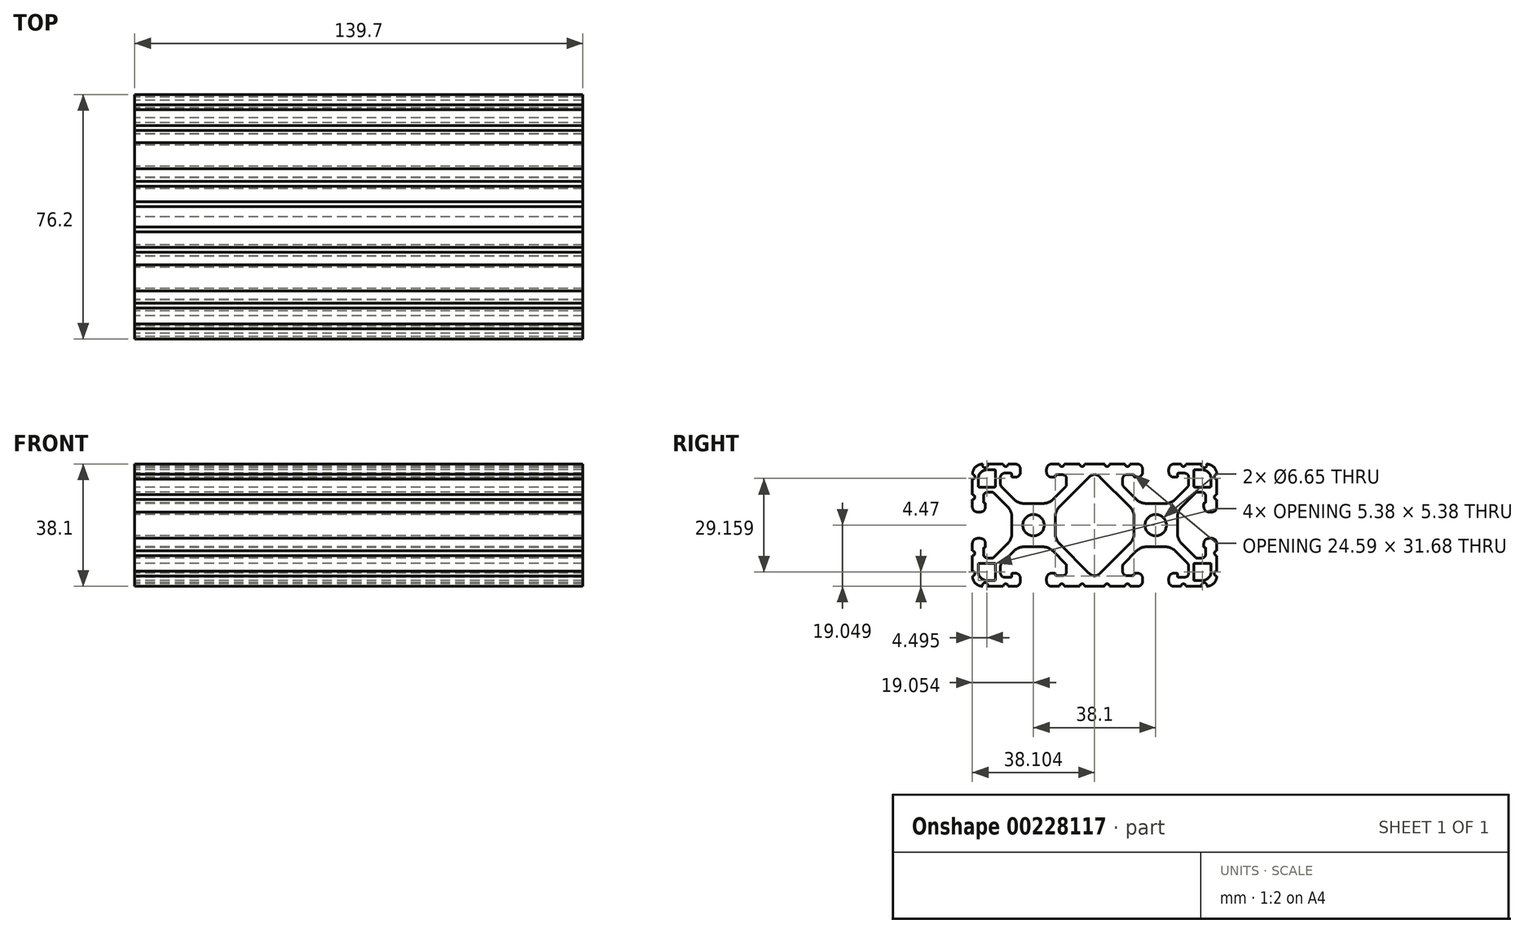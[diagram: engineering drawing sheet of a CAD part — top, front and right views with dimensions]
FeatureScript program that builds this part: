
annotation { "Feature Type Name" : "Feature", "Feature Type Description" : "" }
export const myFeature = defineFeature(function(context is Context, id is Id, definition is map)
    precondition{}
    {
        {
            var Q0;
            Q0=qCreatedBy(makeId("Right.planeOp"),FACE);
            var sketch = newSketch(context, id + "F0", { "sketchPlane" : qUnion([Q0])});
            skArc(sketch, "E0.0.0", {"start": v(-2.87, 19.05) * mm, "mid": v(-3.63, 18.29) * mm, "end": v(-4.4, 19.05) * mm});
            skLineSegment(sketch, "E0.0.1", {"start": v(-4.4, 19.05) * mm, "end": v(-9.22, 19.05) * mm});
            skArc(sketch, "E0.0.2", {"start": v(-9.22, 19.05) * mm, "mid": v(-9.98, 18.29) * mm, "end": v(-10.74, 19.05) * mm});
            skLineSegment(sketch, "E0.0.3", {"start": v(-10.74, 19.05) * mm, "end": v(-13.16, 19.05) * mm});
            skArc(sketch, "E0.0.4", {"start": v(-13.16, 19.05) * mm, "mid": v(-14.27, 18.59) * mm, "end": v(-14.73, 17.47) * mm});
            skLineSegment(sketch, "E0.0.5", {"start": v(-14.73, 17.47) * mm, "end": v(-14.73, 16.56) * mm});
            skArc(sketch, "E0.0.6", {"start": v(-14.73, 16.56) * mm, "mid": v(-14.27, 15.45) * mm, "end": v(-13.16, 14.99) * mm});
            skLineSegment(sketch, "E0.0.7", {"start": v(-13.16, 14.99) * mm, "end": v(-12.22, 14.99) * mm});
            skArc(sketch, "E0.0.8", {"start": v(-12.22, 14.99) * mm, "mid": v(-12.04, 15.06) * mm, "end": v(-11.96, 15.24) * mm});
            skLineSegment(sketch, "E0.0.9", {"start": v(-11.96, 15.24) * mm, "end": v(-11.96, 15.5) * mm});
            skArc(sketch, "E0.0.10", {"start": v(-11.96, 15.5) * mm, "mid": v(-11.89, 15.68) * mm, "end": v(-11.7, 15.75) * mm});
            skLineSegment(sketch, "E0.0.11", {"start": v(-11.7, 15.75) * mm, "end": v(-9.78, 15.75) * mm});
            skArc(sketch, "E0.0.12", {"start": v(-9.78, 15.75) * mm, "mid": v(-8.88, 15.38) * mm, "end": v(-8.5, 14.48) * mm});
            skLineSegment(sketch, "E0.0.13", {"start": v(-8.5, 14.48) * mm, "end": v(-8.5, 12.63) * mm});
            skArc(sketch, "E0.0.14", {"start": v(-8.5, 12.63) * mm, "mid": v(-8.58, 12.3) * mm, "end": v(-8.77, 12) * mm});
            skLineSegment(sketch, "E0.0.15", {"start": v(-8.77, 12) * mm, "end": v(-12.65, 8.12) * mm});
            skArc(sketch, "E0.0.16", {"start": v(-12.65, 8.12) * mm, "mid": v(-14.17, 7.11) * mm, "end": v(-15.95, 6.76) * mm});
            skLineSegment(sketch, "E0.0.17", {"start": v(-15.95, 6.76) * mm, "end": v(-21.69, 6.76) * mm});
            skArc(sketch, "E0.0.18", {"start": v(-21.69, 6.76) * mm, "mid": v(-23.43, 7.1) * mm, "end": v(-24.9, 8.09) * mm});
            skLineSegment(sketch, "E0.0.19", {"start": v(-24.9, 8.09) * mm, "end": v(-28.7, 11.9) * mm});
            skArc(sketch, "E0.0.20", {"start": v(-28.7, 11.9) * mm, "mid": v(-28.99, 12.3) * mm, "end": v(-29.08, 12.8) * mm});
            skLineSegment(sketch, "E0.0.21", {"start": v(-29.08, 12.8) * mm, "end": v(-29.08, 14.95) * mm});
            skArc(sketch, "E0.0.22", {"start": v(-29.08, 14.95) * mm, "mid": v(-28.71, 15.85) * mm, "end": v(-27.81, 16.22) * mm});
            skLineSegment(sketch, "E0.0.23", {"start": v(-27.81, 16.22) * mm, "end": v(-25.88, 16.22) * mm});
            skArc(sketch, "E0.0.24", {"start": v(-25.88, 16.22) * mm, "mid": v(-25.7, 16.14) * mm, "end": v(-25.63, 15.96) * mm});
            skLineSegment(sketch, "E0.0.25", {"start": v(-25.63, 15.96) * mm, "end": v(-25.63, 15.24) * mm});
            skArc(sketch, "E0.0.26", {"start": v(-25.63, 15.24) * mm, "mid": v(-25.56, 15.06) * mm, "end": v(-25.38, 14.99) * mm});
            skLineSegment(sketch, "E0.0.27", {"start": v(-25.38, 14.99) * mm, "end": v(-24.44, 14.99) * mm});
            skArc(sketch, "E0.0.28", {"start": v(-24.44, 14.99) * mm, "mid": v(-23.32, 15.45) * mm, "end": v(-22.86, 16.56) * mm});
            skLineSegment(sketch, "E0.0.29", {"start": v(-22.86, 16.56) * mm, "end": v(-22.86, 17.45) * mm});
            skArc(sketch, "E0.0.30", {"start": v(-22.86, 17.45) * mm, "mid": v(-23.33, 18.58) * mm, "end": v(-24.46, 19.05) * mm});
            skLineSegment(sketch, "E0.0.31", {"start": v(-24.46, 19.05) * mm, "end": v(-26.7, 19.05) * mm});
            skArc(sketch, "E0.0.32", {"start": v(-26.7, 19.05) * mm, "mid": v(-27.45, 18.29) * mm, "end": v(-28.22, 19.05) * mm});
            skLineSegment(sketch, "E0.0.33", {"start": v(-28.22, 19.05) * mm, "end": v(-33.15, 19.05) * mm});
            skArc(sketch, "E0.0.34", {"start": v(-33.15, 19.05) * mm, "mid": v(-33.9, 17.92) * mm, "end": v(-34.64, 19.05) * mm});
            skArc(sketch, "E0.0.35", {"start": v(-34.64, 19.05) * mm, "mid": v(-36.9, 18.11) * mm, "end": v(-37.82, 15.85) * mm});
            skArc(sketch, "E0.0.36", {"start": v(-37.82, 15.85) * mm, "mid": v(-37.07, 15.07) * mm, "end": v(-37.85, 14.32) * mm});
            skLineSegment(sketch, "E0.0.37", {"start": v(-37.85, 14.32) * mm, "end": v(-37.85, 9.5) * mm});
            skArc(sketch, "E0.0.38", {"start": v(-37.85, 9.5) * mm, "mid": v(-37.08, 8.73) * mm, "end": v(-37.85, 7.97) * mm});
            skLineSegment(sketch, "E0.0.39", {"start": v(-37.85, 7.97) * mm, "end": v(-37.85, 5.64) * mm});
            skArc(sketch, "E0.0.40", {"start": v(-37.85, 5.64) * mm, "mid": v(-37.4, 4.56) * mm, "end": v(-36.31, 4.11) * mm});
            skLineSegment(sketch, "E0.0.41", {"start": v(-36.31, 4.11) * mm, "end": v(-35.36, 4.11) * mm});
            skArc(sketch, "E0.0.42", {"start": v(-35.36, 4.11) * mm, "mid": v(-34.24, 4.57) * mm, "end": v(-33.78, 5.69) * mm});
            skLineSegment(sketch, "E0.0.43", {"start": v(-33.78, 5.69) * mm, "end": v(-33.78, 6.7) * mm});
            skArc(sketch, "E0.0.44", {"start": v(-33.78, 6.7) * mm, "mid": v(-33.86, 6.88) * mm, "end": v(-34.04, 6.96) * mm});
            skLineSegment(sketch, "E0.0.45", {"start": v(-34.04, 6.96) * mm, "end": v(-34.14, 6.96) * mm});
            skArc(sketch, "E0.0.46", {"start": v(-34.14, 6.96) * mm, "mid": v(-34.32, 7.03) * mm, "end": v(-34.4, 7.21) * mm});
            skLineSegment(sketch, "E0.0.47", {"start": v(-34.4, 7.21) * mm, "end": v(-34.4, 9.03) * mm});
            skArc(sketch, "E0.0.48", {"start": v(-34.4, 9.03) * mm, "mid": v(-34.02, 9.92) * mm, "end": v(-33.13, 10.3) * mm});
            skLineSegment(sketch, "E0.0.49", {"start": v(-33.13, 10.3) * mm, "end": v(-31.78, 10.3) * mm});
            skArc(sketch, "E0.0.50", {"start": v(-31.78, 10.3) * mm, "mid": v(-31.45, 10.22) * mm, "end": v(-31.17, 10.04) * mm});
            skLineSegment(sketch, "E0.0.51", {"start": v(-31.17, 10.04) * mm, "end": v(-26.94, 5.82) * mm});
            skArc(sketch, "E0.0.52", {"start": v(-26.94, 5.82) * mm, "mid": v(-25.91, 4.27) * mm, "end": v(-25.55, 2.46) * mm});
            skLineSegment(sketch, "E0.0.53", {"start": v(-25.55, 2.46) * mm, "end": v(-25.55, -2.46) * mm});
            skArc(sketch, "E0.0.54", {"start": v(-25.55, -2.46) * mm, "mid": v(-25.91, -4.28) * mm, "end": v(-26.94, -5.82) * mm});
            skLineSegment(sketch, "E0.0.55", {"start": v(-26.94, -5.82) * mm, "end": v(-31.17, -10.04) * mm});
            skArc(sketch, "E0.0.56", {"start": v(-31.17, -10.04) * mm, "mid": v(-31.45, -10.23) * mm, "end": v(-31.78, -10.3) * mm});
            skLineSegment(sketch, "E0.0.57", {"start": v(-31.78, -10.3) * mm, "end": v(-33.13, -10.3) * mm});
            skArc(sketch, "E0.0.58", {"start": v(-33.13, -10.3) * mm, "mid": v(-34.02, -9.92) * mm, "end": v(-34.4, -9.03) * mm});
            skLineSegment(sketch, "E0.0.59", {"start": v(-34.4, -9.03) * mm, "end": v(-34.4, -7.21) * mm});
            skArc(sketch, "E0.0.60", {"start": v(-34.4, -7.21) * mm, "mid": v(-34.32, -7.03) * mm, "end": v(-34.14, -6.96) * mm});
            skLineSegment(sketch, "E0.0.61", {"start": v(-34.14, -6.96) * mm, "end": v(-34.04, -6.96) * mm});
            skArc(sketch, "E0.0.62", {"start": v(-34.04, -6.96) * mm, "mid": v(-33.86, -6.89) * mm, "end": v(-33.78, -6.7) * mm});
            skLineSegment(sketch, "E0.0.63", {"start": v(-33.78, -6.7) * mm, "end": v(-33.78, -5.69) * mm});
            skArc(sketch, "E0.0.64", {"start": v(-33.78, -5.69) * mm, "mid": v(-34.24, -4.57) * mm, "end": v(-35.36, -4.11) * mm});
            skLineSegment(sketch, "E0.0.65", {"start": v(-35.36, -4.11) * mm, "end": v(-36.31, -4.11) * mm});
            skArc(sketch, "E0.0.66", {"start": v(-36.31, -4.11) * mm, "mid": v(-37.4, -4.56) * mm, "end": v(-37.85, -5.65) * mm});
            skLineSegment(sketch, "E0.0.67", {"start": v(-37.85, -5.65) * mm, "end": v(-37.85, -7.97) * mm});
            skArc(sketch, "E0.0.68", {"start": v(-37.85, -7.97) * mm, "mid": v(-37.08, -8.74) * mm, "end": v(-37.85, -9.5) * mm});
            skLineSegment(sketch, "E0.0.69", {"start": v(-37.85, -9.5) * mm, "end": v(-37.85, -14.33) * mm});
            skArc(sketch, "E0.0.70", {"start": v(-37.85, -14.33) * mm, "mid": v(-37.07, -15.08) * mm, "end": v(-37.82, -15.85) * mm});
            skArc(sketch, "E0.0.71", {"start": v(-37.82, -15.85) * mm, "mid": v(-36.9, -18.12) * mm, "end": v(-34.64, -19.05) * mm});
            skArc(sketch, "E0.0.72", {"start": v(-34.64, -19.05) * mm, "mid": v(-33.9, -17.92) * mm, "end": v(-33.15, -19.05) * mm});
            skLineSegment(sketch, "E0.0.73", {"start": v(-33.15, -19.05) * mm, "end": v(-28.22, -19.05) * mm});
            skArc(sketch, "E0.0.74", {"start": v(-28.22, -19.05) * mm, "mid": v(-27.45, -18.29) * mm, "end": v(-26.7, -19.05) * mm});
            skLineSegment(sketch, "E0.0.75", {"start": v(-26.7, -19.05) * mm, "end": v(-24.46, -19.05) * mm});
            skArc(sketch, "E0.0.76", {"start": v(-24.46, -19.05) * mm, "mid": v(-23.33, -18.58) * mm, "end": v(-22.86, -17.45) * mm});
            skLineSegment(sketch, "E0.0.77", {"start": v(-22.86, -17.45) * mm, "end": v(-22.86, -16.56) * mm});
            skArc(sketch, "E0.0.78", {"start": v(-22.86, -16.56) * mm, "mid": v(-23.32, -15.45) * mm, "end": v(-24.44, -14.99) * mm});
            skLineSegment(sketch, "E0.0.79", {"start": v(-24.44, -14.99) * mm, "end": v(-25.38, -14.99) * mm});
            skArc(sketch, "E0.0.80", {"start": v(-25.38, -14.99) * mm, "mid": v(-25.56, -15.06) * mm, "end": v(-25.63, -15.24) * mm});
            skLineSegment(sketch, "E0.0.81", {"start": v(-25.63, -15.24) * mm, "end": v(-25.63, -15.97) * mm});
            skArc(sketch, "E0.0.82", {"start": v(-25.63, -15.97) * mm, "mid": v(-25.7, -16.15) * mm, "end": v(-25.88, -16.22) * mm});
            skLineSegment(sketch, "E0.0.83", {"start": v(-25.88, -16.22) * mm, "end": v(-27.81, -16.22) * mm});
            skArc(sketch, "E0.0.84", {"start": v(-27.81, -16.22) * mm, "mid": v(-28.71, -15.85) * mm, "end": v(-29.08, -14.95) * mm});
            skLineSegment(sketch, "E0.0.85", {"start": v(-29.08, -14.95) * mm, "end": v(-29.08, -12.8) * mm});
            skArc(sketch, "E0.0.86", {"start": v(-29.08, -12.8) * mm, "mid": v(-28.99, -12.3) * mm, "end": v(-28.7, -11.9) * mm});
            skLineSegment(sketch, "E0.0.87", {"start": v(-28.7, -11.9) * mm, "end": v(-24.9, -8.1) * mm});
            skArc(sketch, "E0.0.88", {"start": v(-24.9, -8.1) * mm, "mid": v(-23.43, -7.1) * mm, "end": v(-21.69, -6.76) * mm});
            skLineSegment(sketch, "E0.0.89", {"start": v(-21.69, -6.76) * mm, "end": v(-15.95, -6.76) * mm});
            skArc(sketch, "E0.0.90", {"start": v(-15.95, -6.76) * mm, "mid": v(-14.17, -7.11) * mm, "end": v(-12.65, -8.13) * mm});
            skLineSegment(sketch, "E0.0.91", {"start": v(-12.65, -8.13) * mm, "end": v(-8.77, -12) * mm});
            skArc(sketch, "E0.0.92", {"start": v(-8.77, -12) * mm, "mid": v(-8.58, -12.3) * mm, "end": v(-8.5, -12.64) * mm});
            skLineSegment(sketch, "E0.0.93", {"start": v(-8.5, -12.64) * mm, "end": v(-8.5, -14.48) * mm});
            skArc(sketch, "E0.0.94", {"start": v(-8.5, -14.48) * mm, "mid": v(-8.88, -15.38) * mm, "end": v(-9.78, -15.75) * mm});
            skLineSegment(sketch, "E0.0.95", {"start": v(-9.78, -15.75) * mm, "end": v(-11.7, -15.75) * mm});
            skArc(sketch, "E0.0.96", {"start": v(-11.7, -15.75) * mm, "mid": v(-11.89, -15.68) * mm, "end": v(-11.96, -15.5) * mm});
            skLineSegment(sketch, "E0.0.97", {"start": v(-11.96, -15.5) * mm, "end": v(-11.96, -15.24) * mm});
            skArc(sketch, "E0.0.98", {"start": v(-11.96, -15.24) * mm, "mid": v(-12.04, -15.06) * mm, "end": v(-12.22, -14.99) * mm});
            skLineSegment(sketch, "E0.0.99", {"start": v(-12.22, -14.99) * mm, "end": v(-13.16, -14.99) * mm});
            skArc(sketch, "E0.0.100", {"start": v(-13.16, -14.99) * mm, "mid": v(-14.27, -15.45) * mm, "end": v(-14.73, -16.56) * mm});
            skLineSegment(sketch, "E0.0.101", {"start": v(-14.73, -16.56) * mm, "end": v(-14.73, -17.48) * mm});
            skArc(sketch, "E0.0.102", {"start": v(-14.73, -17.48) * mm, "mid": v(-14.27, -18.59) * mm, "end": v(-13.16, -19.05) * mm});
            skLineSegment(sketch, "E0.0.103", {"start": v(-13.16, -19.05) * mm, "end": v(-10.74, -19.05) * mm});
            skArc(sketch, "E0.0.104", {"start": v(-10.74, -19.05) * mm, "mid": v(-9.98, -18.29) * mm, "end": v(-9.22, -19.05) * mm});
            skLineSegment(sketch, "E0.0.105", {"start": v(-9.22, -19.05) * mm, "end": v(-4.4, -19.05) * mm});
            skArc(sketch, "E0.0.106", {"start": v(-4.4, -19.05) * mm, "mid": v(-3.63, -18.29) * mm, "end": v(-2.87, -19.05) * mm});
            skLineSegment(sketch, "E0.0.107", {"start": v(-2.87, -19.05) * mm, "end": v(3.38, -19.05) * mm});
            skArc(sketch, "E0.0.108", {"start": v(3.38, -19.05) * mm, "mid": v(4.14, -18.29) * mm, "end": v(4.9, -19.05) * mm});
            skLineSegment(sketch, "E0.0.109", {"start": v(4.9, -19.05) * mm, "end": v(9.73, -19.05) * mm});
            skArc(sketch, "E0.0.110", {"start": v(9.73, -19.05) * mm, "mid": v(10.49, -18.29) * mm, "end": v(11.25, -19.05) * mm});
            skLineSegment(sketch, "E0.0.111", {"start": v(11.25, -19.05) * mm, "end": v(13.66, -19.05) * mm});
            skArc(sketch, "E0.0.112", {"start": v(13.66, -19.05) * mm, "mid": v(14.78, -18.59) * mm, "end": v(15.24, -17.48) * mm});
            skLineSegment(sketch, "E0.0.113", {"start": v(15.24, -17.48) * mm, "end": v(15.24, -16.56) * mm});
            skArc(sketch, "E0.0.114", {"start": v(15.24, -16.56) * mm, "mid": v(14.78, -15.45) * mm, "end": v(13.66, -14.99) * mm});
            skLineSegment(sketch, "E0.0.115", {"start": v(13.66, -14.99) * mm, "end": v(12.72, -14.99) * mm});
            skArc(sketch, "E0.0.116", {"start": v(12.72, -14.99) * mm, "mid": v(12.54, -15.06) * mm, "end": v(12.47, -15.24) * mm});
            skLineSegment(sketch, "E0.0.117", {"start": v(12.47, -15.24) * mm, "end": v(12.47, -15.5) * mm});
            skArc(sketch, "E0.0.118", {"start": v(12.47, -15.5) * mm, "mid": v(12.4, -15.68) * mm, "end": v(12.22, -15.75) * mm});
            skLineSegment(sketch, "E0.0.119", {"start": v(12.22, -15.75) * mm, "end": v(10.29, -15.75) * mm});
            skArc(sketch, "E0.0.120", {"start": v(10.29, -15.75) * mm, "mid": v(9.39, -15.38) * mm, "end": v(9.02, -14.48) * mm});
            skLineSegment(sketch, "E0.0.121", {"start": v(9.02, -14.48) * mm, "end": v(9.02, -12.64) * mm});
            skArc(sketch, "E0.0.122", {"start": v(9.02, -12.64) * mm, "mid": v(9.08, -12.3) * mm, "end": v(9.28, -12) * mm});
            skLineSegment(sketch, "E0.0.123", {"start": v(9.28, -12) * mm, "end": v(13.16, -8.13) * mm});
            skArc(sketch, "E0.0.124", {"start": v(13.16, -8.13) * mm, "mid": v(14.67, -7.11) * mm, "end": v(16.46, -6.76) * mm});
            skLineSegment(sketch, "E0.0.125", {"start": v(16.46, -6.76) * mm, "end": v(22.2, -6.76) * mm});
            skArc(sketch, "E0.0.126", {"start": v(22.2, -6.76) * mm, "mid": v(23.94, -7.1) * mm, "end": v(25.42, -8.1) * mm});
            skLineSegment(sketch, "E0.0.127", {"start": v(25.42, -8.1) * mm, "end": v(29.22, -11.9) * mm});
            skArc(sketch, "E0.0.128", {"start": v(29.22, -11.9) * mm, "mid": v(29.5, -12.3) * mm, "end": v(29.6, -12.8) * mm});
            skLineSegment(sketch, "E0.0.129", {"start": v(29.6, -12.8) * mm, "end": v(29.6, -14.95) * mm});
            skArc(sketch, "E0.0.130", {"start": v(29.6, -14.95) * mm, "mid": v(29.22, -15.85) * mm, "end": v(28.32, -16.22) * mm});
            skLineSegment(sketch, "E0.0.131", {"start": v(28.32, -16.22) * mm, "end": v(26.4, -16.22) * mm});
            skArc(sketch, "E0.0.132", {"start": v(26.4, -16.22) * mm, "mid": v(26.21, -16.15) * mm, "end": v(26.14, -15.97) * mm});
            skLineSegment(sketch, "E0.0.133", {"start": v(26.14, -15.97) * mm, "end": v(26.14, -15.24) * mm});
            skArc(sketch, "E0.0.134", {"start": v(26.14, -15.24) * mm, "mid": v(26.06, -15.06) * mm, "end": v(25.88, -14.99) * mm});
            skLineSegment(sketch, "E0.0.135", {"start": v(25.88, -14.99) * mm, "end": v(24.94, -14.99) * mm});
            skArc(sketch, "E0.0.136", {"start": v(24.94, -14.99) * mm, "mid": v(23.83, -15.45) * mm, "end": v(23.37, -16.56) * mm});
            skLineSegment(sketch, "E0.0.137", {"start": v(23.37, -16.56) * mm, "end": v(23.37, -17.45) * mm});
            skArc(sketch, "E0.0.138", {"start": v(23.37, -17.45) * mm, "mid": v(23.84, -18.58) * mm, "end": v(24.97, -19.05) * mm});
            skLineSegment(sketch, "E0.0.139", {"start": v(24.97, -19.05) * mm, "end": v(27.2, -19.05) * mm});
            skArc(sketch, "E0.0.140", {"start": v(27.2, -19.05) * mm, "mid": v(27.96, -18.29) * mm, "end": v(28.72, -19.05) * mm});
            skLineSegment(sketch, "E0.0.141", {"start": v(28.72, -19.05) * mm, "end": v(33.65, -19.05) * mm});
            skArc(sketch, "E0.0.142", {"start": v(33.65, -19.05) * mm, "mid": v(34.4, -17.92) * mm, "end": v(35.15, -19.05) * mm});
            skArc(sketch, "E0.0.143", {"start": v(35.15, -19.05) * mm, "mid": v(37.4, -18.12) * mm, "end": v(38.33, -15.85) * mm});
            skArc(sketch, "E0.0.144", {"start": v(38.33, -15.85) * mm, "mid": v(37.58, -15.08) * mm, "end": v(38.35, -14.33) * mm});
            skLineSegment(sketch, "E0.0.145", {"start": v(38.35, -14.33) * mm, "end": v(38.35, -9.5) * mm});
            skArc(sketch, "E0.0.146", {"start": v(38.35, -9.5) * mm, "mid": v(37.6, -8.74) * mm, "end": v(38.35, -7.97) * mm});
            skLineSegment(sketch, "E0.0.147", {"start": v(38.35, -7.97) * mm, "end": v(38.35, -5.65) * mm});
            skArc(sketch, "E0.0.148", {"start": v(38.35, -5.65) * mm, "mid": v(37.9, -4.56) * mm, "end": v(36.82, -4.11) * mm});
            skLineSegment(sketch, "E0.0.149", {"start": v(36.82, -4.11) * mm, "end": v(35.86, -4.11) * mm});
            skArc(sketch, "E0.0.150", {"start": v(35.86, -4.11) * mm, "mid": v(34.75, -4.57) * mm, "end": v(34.29, -5.69) * mm});
            skLineSegment(sketch, "E0.0.151", {"start": v(34.29, -5.69) * mm, "end": v(34.29, -6.7) * mm});
            skArc(sketch, "E0.0.152", {"start": v(34.29, -6.7) * mm, "mid": v(34.36, -6.89) * mm, "end": v(34.54, -6.96) * mm});
            skLineSegment(sketch, "E0.0.153", {"start": v(34.54, -6.96) * mm, "end": v(34.65, -6.96) * mm});
            skArc(sketch, "E0.0.154", {"start": v(34.65, -6.96) * mm, "mid": v(34.83, -7.03) * mm, "end": v(34.9, -7.21) * mm});
            skLineSegment(sketch, "E0.0.155", {"start": v(34.9, -7.21) * mm, "end": v(34.9, -9.03) * mm});
            skArc(sketch, "E0.0.156", {"start": v(34.9, -9.03) * mm, "mid": v(34.53, -9.92) * mm, "end": v(33.64, -10.3) * mm});
            skLineSegment(sketch, "E0.0.157", {"start": v(33.64, -10.3) * mm, "end": v(32.29, -10.3) * mm});
            skArc(sketch, "E0.0.158", {"start": v(32.29, -10.3) * mm, "mid": v(31.95, -10.23) * mm, "end": v(31.67, -10.04) * mm});
            skLineSegment(sketch, "E0.0.159", {"start": v(31.67, -10.04) * mm, "end": v(27.45, -5.82) * mm});
            skArc(sketch, "E0.0.160", {"start": v(27.45, -5.82) * mm, "mid": v(26.42, -4.28) * mm, "end": v(26.06, -2.46) * mm});
            skLineSegment(sketch, "E0.0.161", {"start": v(26.06, -2.46) * mm, "end": v(26.06, 2.46) * mm});
            skArc(sketch, "E0.0.162", {"start": v(26.06, 2.46) * mm, "mid": v(26.42, 4.27) * mm, "end": v(27.45, 5.82) * mm});
            skLineSegment(sketch, "E0.0.163", {"start": v(27.45, 5.82) * mm, "end": v(31.67, 10.04) * mm});
            skArc(sketch, "E0.0.164", {"start": v(31.67, 10.04) * mm, "mid": v(31.95, 10.22) * mm, "end": v(32.29, 10.3) * mm});
            skLineSegment(sketch, "E0.0.165", {"start": v(32.29, 10.3) * mm, "end": v(33.64, 10.3) * mm});
            skArc(sketch, "E0.0.166", {"start": v(33.64, 10.3) * mm, "mid": v(34.53, 9.92) * mm, "end": v(34.9, 9.03) * mm});
            skLineSegment(sketch, "E0.0.167", {"start": v(34.9, 9.03) * mm, "end": v(34.9, 7.21) * mm});
            skArc(sketch, "E0.0.168", {"start": v(34.9, 7.21) * mm, "mid": v(34.83, 7.03) * mm, "end": v(34.65, 6.96) * mm});
            skLineSegment(sketch, "E0.0.169", {"start": v(34.65, 6.96) * mm, "end": v(34.54, 6.96) * mm});
            skArc(sketch, "E0.0.170", {"start": v(34.54, 6.96) * mm, "mid": v(34.36, 6.88) * mm, "end": v(34.29, 6.7) * mm});
            skLineSegment(sketch, "E0.0.171", {"start": v(34.29, 6.7) * mm, "end": v(34.29, 5.69) * mm});
            skArc(sketch, "E0.0.172", {"start": v(34.29, 5.69) * mm, "mid": v(34.75, 4.57) * mm, "end": v(35.86, 4.11) * mm});
            skLineSegment(sketch, "E0.0.173", {"start": v(35.86, 4.11) * mm, "end": v(36.82, 4.11) * mm});
            skArc(sketch, "E0.0.174", {"start": v(36.82, 4.11) * mm, "mid": v(37.9, 4.56) * mm, "end": v(38.35, 5.64) * mm});
            skLineSegment(sketch, "E0.0.175", {"start": v(38.35, 5.64) * mm, "end": v(38.35, 7.97) * mm});
            skArc(sketch, "E0.0.176", {"start": v(38.35, 7.97) * mm, "mid": v(37.6, 8.73) * mm, "end": v(38.35, 9.5) * mm});
            skLineSegment(sketch, "E0.0.177", {"start": v(38.35, 9.5) * mm, "end": v(38.35, 14.32) * mm});
            skArc(sketch, "E0.0.178", {"start": v(38.35, 14.32) * mm, "mid": v(37.58, 15.07) * mm, "end": v(38.33, 15.85) * mm});
            skArc(sketch, "E0.0.179", {"start": v(38.33, 15.85) * mm, "mid": v(37.4, 18.11) * mm, "end": v(35.15, 19.05) * mm});
            skArc(sketch, "E0.0.180", {"start": v(35.15, 19.05) * mm, "mid": v(34.4, 17.92) * mm, "end": v(33.65, 19.05) * mm});
            skLineSegment(sketch, "E0.0.181", {"start": v(33.65, 19.05) * mm, "end": v(28.72, 19.05) * mm});
            skArc(sketch, "E0.0.182", {"start": v(28.72, 19.05) * mm, "mid": v(27.96, 18.29) * mm, "end": v(27.2, 19.05) * mm});
            skLineSegment(sketch, "E0.0.183", {"start": v(27.2, 19.05) * mm, "end": v(24.97, 19.05) * mm});
            skArc(sketch, "E0.0.184", {"start": v(24.97, 19.05) * mm, "mid": v(23.84, 18.58) * mm, "end": v(23.37, 17.45) * mm});
            skLineSegment(sketch, "E0.0.185", {"start": v(23.37, 17.45) * mm, "end": v(23.37, 16.56) * mm});
            skArc(sketch, "E0.0.186", {"start": v(23.37, 16.56) * mm, "mid": v(23.83, 15.45) * mm, "end": v(24.94, 14.99) * mm});
            skLineSegment(sketch, "E0.0.187", {"start": v(24.94, 14.99) * mm, "end": v(25.88, 14.99) * mm});
            skArc(sketch, "E0.0.188", {"start": v(25.88, 14.99) * mm, "mid": v(26.06, 15.06) * mm, "end": v(26.14, 15.24) * mm});
            skLineSegment(sketch, "E0.0.189", {"start": v(26.14, 15.24) * mm, "end": v(26.14, 15.96) * mm});
            skArc(sketch, "E0.0.190", {"start": v(26.14, 15.96) * mm, "mid": v(26.21, 16.14) * mm, "end": v(26.4, 16.22) * mm});
            skLineSegment(sketch, "E0.0.191", {"start": v(26.4, 16.22) * mm, "end": v(28.32, 16.22) * mm});
            skArc(sketch, "E0.0.192", {"start": v(28.32, 16.22) * mm, "mid": v(29.22, 15.85) * mm, "end": v(29.6, 14.95) * mm});
            skLineSegment(sketch, "E0.0.193", {"start": v(29.6, 14.95) * mm, "end": v(29.6, 12.8) * mm});
            skArc(sketch, "E0.0.194", {"start": v(29.6, 12.8) * mm, "mid": v(29.5, 12.3) * mm, "end": v(29.22, 11.9) * mm});
            skLineSegment(sketch, "E0.0.195", {"start": v(29.22, 11.9) * mm, "end": v(25.42, 8.09) * mm});
            skArc(sketch, "E0.0.196", {"start": v(25.42, 8.09) * mm, "mid": v(23.94, 7.1) * mm, "end": v(22.2, 6.76) * mm});
            skLineSegment(sketch, "E0.0.197", {"start": v(22.2, 6.76) * mm, "end": v(16.46, 6.76) * mm});
            skArc(sketch, "E0.0.198", {"start": v(16.46, 6.76) * mm, "mid": v(14.67, 7.11) * mm, "end": v(13.16, 8.12) * mm});
            skLineSegment(sketch, "E0.0.199", {"start": v(13.16, 8.12) * mm, "end": v(9.28, 12) * mm});
            skArc(sketch, "E0.0.200", {"start": v(9.28, 12) * mm, "mid": v(9.08, 12.3) * mm, "end": v(9.02, 12.63) * mm});
            skLineSegment(sketch, "E0.0.201", {"start": v(9.02, 12.63) * mm, "end": v(9.02, 14.48) * mm});
            skArc(sketch, "E0.0.202", {"start": v(9.02, 14.48) * mm, "mid": v(9.39, 15.38) * mm, "end": v(10.29, 15.75) * mm});
            skLineSegment(sketch, "E0.0.203", {"start": v(10.29, 15.75) * mm, "end": v(12.22, 15.75) * mm});
            skArc(sketch, "E0.0.204", {"start": v(12.22, 15.75) * mm, "mid": v(12.4, 15.68) * mm, "end": v(12.47, 15.5) * mm});
            skLineSegment(sketch, "E0.0.205", {"start": v(12.47, 15.5) * mm, "end": v(12.47, 15.24) * mm});
            skArc(sketch, "E0.0.206", {"start": v(12.47, 15.24) * mm, "mid": v(12.54, 15.06) * mm, "end": v(12.72, 14.99) * mm});
            skLineSegment(sketch, "E0.0.207", {"start": v(12.72, 14.99) * mm, "end": v(13.66, 14.99) * mm});
            skArc(sketch, "E0.0.208", {"start": v(13.66, 14.99) * mm, "mid": v(14.78, 15.45) * mm, "end": v(15.24, 16.56) * mm});
            skLineSegment(sketch, "E0.0.209", {"start": v(15.24, 16.56) * mm, "end": v(15.24, 17.47) * mm});
            skArc(sketch, "E0.0.210", {"start": v(15.24, 17.47) * mm, "mid": v(14.78, 18.59) * mm, "end": v(13.66, 19.05) * mm});
            skLineSegment(sketch, "E0.0.211", {"start": v(13.66, 19.05) * mm, "end": v(11.25, 19.05) * mm});
            skArc(sketch, "E0.0.212", {"start": v(11.25, 19.05) * mm, "mid": v(10.49, 18.29) * mm, "end": v(9.73, 19.05) * mm});
            skLineSegment(sketch, "E0.0.213", {"start": v(9.73, 19.05) * mm, "end": v(4.9, 19.05) * mm});
            skArc(sketch, "E0.0.214", {"start": v(4.9, 19.05) * mm, "mid": v(4.14, 18.29) * mm, "end": v(3.38, 19.05) * mm});
            skLineSegment(sketch, "E0.0.215", {"start": v(3.38, 19.05) * mm, "end": v(-2.87, 19.05) * mm});
            skLineSegment(sketch, "E1.0", {"start": v(-30.66, 12.14) * mm, "end": v(-30.66, 17.02) * mm});
            skArc(sketch, "E1.1", {"start": v(-30.92, 11.89) * mm, "mid": v(-30.74, 11.96) * mm, "end": v(-30.66, 12.14) * mm});
            skLineSegment(sketch, "E1.2", {"start": v(-35.8, 11.89) * mm, "end": v(-30.92, 11.89) * mm});
            skLineSegment(sketch, "E1.4", {"start": v(-36.05, 14.48) * mm, "end": v(-36.05, 12.14) * mm});
            skPoint(sketch, "E1.5", {"position": v(-36.05, 12.14) * mm});
            skArc(sketch, "E1.6", {"start": v(-36.05, 12.14) * mm, "mid": v(-35.97, 11.96) * mm, "end": v(-35.8, 11.89) * mm});
            skArc(sketch, "E1.7", {"start": v(-33.25, 17.27) * mm, "mid": v(-35.23, 16.45) * mm, "end": v(-36.05, 14.48) * mm});
            skLineSegment(sketch, "E1.8", {"start": v(-30.92, 17.27) * mm, "end": v(-33.25, 17.27) * mm});
            skArc(sketch, "E1.9", {"start": v(-30.66, 17.02) * mm, "mid": v(-30.74, 17.2) * mm, "end": v(-30.92, 17.27) * mm});
            skCircle(sketch, "E1.10", {"center": v(-18.8, 0) * mm, "radius": 3.33 * mm});
            skLineSegment(sketch, "E1.11", {"start": v(-30.66, -17.02) * mm, "end": v(-30.66, -12.14) * mm});
            skArc(sketch, "E1.12", {"start": v(-30.92, -17.27) * mm, "mid": v(-30.74, -17.2) * mm, "end": v(-30.66, -17.02) * mm});
            skLineSegment(sketch, "E1.13", {"start": v(-33.25, -17.27) * mm, "end": v(-30.92, -17.27) * mm});
            skArc(sketch, "E1.14", {"start": v(-36.05, -14.48) * mm, "mid": v(-35.23, -16.45) * mm, "end": v(-33.25, -17.27) * mm});
            skLineSegment(sketch, "E1.15", {"start": v(-36.05, -12.14) * mm, "end": v(-36.05, -14.48) * mm});
            skArc(sketch, "E1.16", {"start": v(-35.8, -11.89) * mm, "mid": v(-35.97, -11.96) * mm, "end": v(-36.05, -12.14) * mm});
            skLineSegment(sketch, "E1.17", {"start": v(-30.92, -11.89) * mm, "end": v(-35.8, -11.89) * mm});
            skPoint(sketch, "E1.18", {"position": v(-30.92, -11.89) * mm});
            skArc(sketch, "E1.19", {"start": v(-30.66, -12.14) * mm, "mid": v(-30.74, -11.96) * mm, "end": v(-30.92, -11.89) * mm});
            skArc(sketch, "E2.0", {"start": v(0.25, -15.84) * mm, "mid": v(1.22, -15.53) * mm, "end": v(2.03, -14.94) * mm});
            skArc(sketch, "E2.1", {"start": v(-1.53, -14.94) * mm, "mid": v(-0.7, -15.53) * mm, "end": v(0.25, -15.84) * mm});
            skLineSegment(sketch, "E2.2", {"start": v(-10.65, -5.82) * mm, "end": v(-1.53, -14.94) * mm});
            skArc(sketch, "E2.3", {"start": v(-12.04, -2.46) * mm, "mid": v(-11.68, -4.28) * mm, "end": v(-10.65, -5.82) * mm});
            skLineSegment(sketch, "E2.4", {"start": v(-12.04, 2.46) * mm, "end": v(-12.04, -2.46) * mm});
            skArc(sketch, "E2.5", {"start": v(-10.65, 5.82) * mm, "mid": v(-11.68, 4.27) * mm, "end": v(-12.04, 2.46) * mm});
            skLineSegment(sketch, "E2.6", {"start": v(-1.53, 14.94) * mm, "end": v(-10.65, 5.82) * mm});
            skArc(sketch, "E2.7", {"start": v(0.25, 15.84) * mm, "mid": v(-0.7, 15.53) * mm, "end": v(-1.53, 14.94) * mm});
            skArc(sketch, "E2.8", {"start": v(2.03, 14.94) * mm, "mid": v(1.22, 15.53) * mm, "end": v(0.25, 15.84) * mm});
            skLineSegment(sketch, "E2.9", {"start": v(11.16, 5.82) * mm, "end": v(2.03, 14.94) * mm});
            skArc(sketch, "E2.10", {"start": v(12.55, 2.46) * mm, "mid": v(12.19, 4.27) * mm, "end": v(11.16, 5.82) * mm});
            skLineSegment(sketch, "E2.11", {"start": v(12.55, -2.46) * mm, "end": v(12.55, 2.46) * mm});
            skArc(sketch, "E2.12", {"start": v(11.16, -5.82) * mm, "mid": v(12.19, -4.28) * mm, "end": v(12.55, -2.46) * mm});
            skLineSegment(sketch, "E2.13", {"start": v(2.03, -14.94) * mm, "end": v(11.16, -5.82) * mm});
            skCircle(sketch, "E2.14", {"center": v(19.3, 0) * mm, "radius": 3.33 * mm});
            skLineSegment(sketch, "E2.15", {"start": v(36.56, -14.48) * mm, "end": v(36.56, -12.14) * mm});
            skArc(sketch, "E2.16", {"start": v(36.56, -12.14) * mm, "mid": v(36.48, -11.96) * mm, "end": v(36.3, -11.89) * mm});
            skLineSegment(sketch, "E2.17", {"start": v(36.3, -11.89) * mm, "end": v(31.42, -11.89) * mm});
            skArc(sketch, "E2.18", {"start": v(31.42, -11.89) * mm, "mid": v(31.24, -11.96) * mm, "end": v(31.17, -12.14) * mm});
            skLineSegment(sketch, "E2.19", {"start": v(31.17, -12.14) * mm, "end": v(31.17, -17.02) * mm});
            skArc(sketch, "E2.20", {"start": v(31.17, -17.02) * mm, "mid": v(31.24, -17.2) * mm, "end": v(31.42, -17.27) * mm});
            skLineSegment(sketch, "E2.21", {"start": v(31.42, -17.27) * mm, "end": v(33.76, -17.27) * mm});
            skArc(sketch, "E2.22", {"start": v(33.76, -17.27) * mm, "mid": v(35.74, -16.45) * mm, "end": v(36.56, -14.48) * mm});
            skLineSegment(sketch, "E2.23", {"start": v(31.42, 11.89) * mm, "end": v(36.3, 11.89) * mm});
            skArc(sketch, "E2.24", {"start": v(36.3, 11.89) * mm, "mid": v(36.48, 11.96) * mm, "end": v(36.56, 12.14) * mm});
            skLineSegment(sketch, "E2.25", {"start": v(36.56, 12.14) * mm, "end": v(36.56, 14.48) * mm});
            skArc(sketch, "E2.26", {"start": v(36.56, 14.48) * mm, "mid": v(35.74, 16.45) * mm, "end": v(33.76, 17.27) * mm});
            skLineSegment(sketch, "E2.27", {"start": v(33.76, 17.27) * mm, "end": v(31.42, 17.27) * mm});
            skArc(sketch, "E2.28", {"start": v(31.42, 17.27) * mm, "mid": v(31.24, 17.2) * mm, "end": v(31.17, 17.02) * mm});
            skLineSegment(sketch, "E2.29", {"start": v(31.17, 17.02) * mm, "end": v(31.17, 12.14) * mm});
            skArc(sketch, "E2.30", {"start": v(31.17, 12.14) * mm, "mid": v(31.24, 11.96) * mm, "end": v(31.42, 11.89) * mm});
            skSolve(sketch);
        }
        {
            var Q0;
            Q0=qSketchRegion(id+"F0",true);
            extrude(context, id + "F1", {"entities" : qUnion([Q0]), "depth" : 139.7 * mm, "symmetric" : true});
        }
    });
